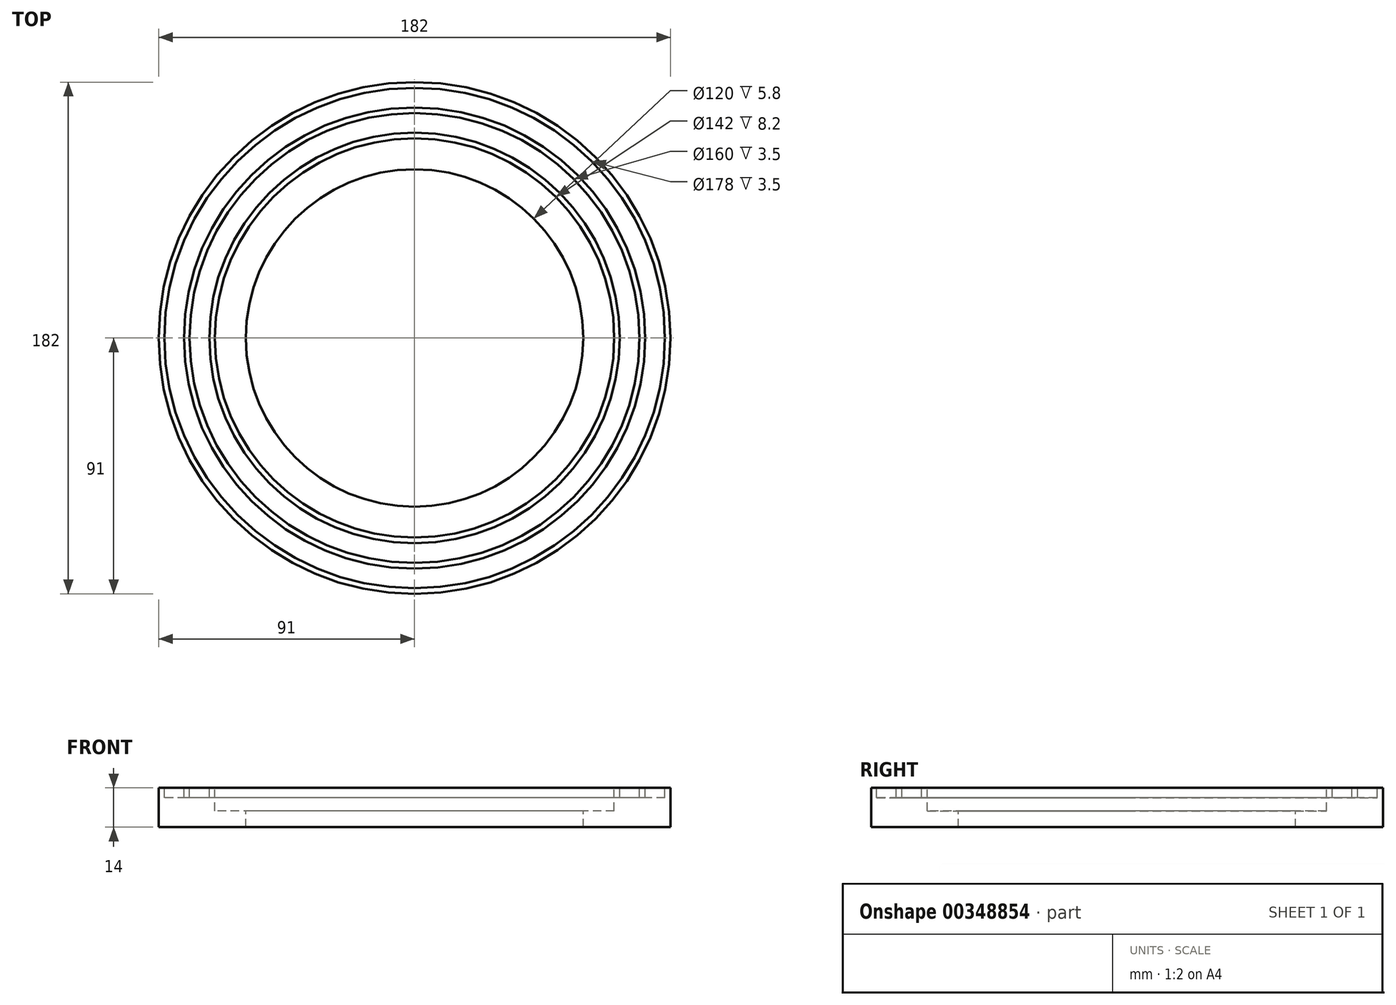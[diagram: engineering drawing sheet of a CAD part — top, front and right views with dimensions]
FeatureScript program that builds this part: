
annotation { "Feature Type Name" : "Feature", "Feature Type Description" : "" }
export const myFeature = defineFeature(function(context is Context, id is Id, definition is map)
    precondition{}
    {
        {
            var Q0;
            Q0=qCreatedBy(makeId("Front.planeOp"),FACE);
            var sketch = newSketch(context, id + "F0", { "sketchPlane" : qUnion([Q0])});
            skLineSegment(sketch, "E0", {"start": v(-60, 0) * mm, "end": v(-58.12, 0) * mm, "construction": true});
            skLineSegment(sketch, "E1", {"start": v(0, 63.7) * mm, "end": v(0, -49.54) * mm, "construction": true});
            skLineSegment(sketch, "E2", {"start": v(-60, 0) * mm, "end": v(-91, 0) * mm});
            skLineSegment(sketch, "E3", {"start": v(-91, 0) * mm, "end": v(-91, 14) * mm});
            skLineSegment(sketch, "E4", {"start": v(-91, 14) * mm, "end": v(-89, 14) * mm});
            skLineSegment(sketch, "E5", {"start": v(-89, 14) * mm, "end": v(-89, 10.5) * mm});
            skLineSegment(sketch, "E6", {"start": v(-89, 10.5) * mm, "end": v(-82, 10.5) * mm});
            skLineSegment(sketch, "E7", {"start": v(-82, 10.5) * mm, "end": v(-82, 14) * mm});
            skLineSegment(sketch, "E8", {"start": v(-82, 14) * mm, "end": v(-80, 14) * mm});
            skLineSegment(sketch, "E9", {"start": v(-80, 14) * mm, "end": v(-80, 10.5) * mm});
            skLineSegment(sketch, "E10", {"start": v(-80, 10.5) * mm, "end": v(-73, 10.5) * mm});
            skLineSegment(sketch, "E11", {"start": v(-73, 10.5) * mm, "end": v(-73, 14) * mm});
            skLineSegment(sketch, "E12", {"start": v(-73, 14) * mm, "end": v(-71, 14) * mm});
            skLineSegment(sketch, "E13", {"start": v(-71, 14) * mm, "end": v(-71, 5.8) * mm});
            skLineSegment(sketch, "E14", {"start": v(-71, 5.8) * mm, "end": v(-60, 5.8) * mm});
            skLineSegment(sketch, "E15", {"start": v(-60, 5.8) * mm, "end": v(-60, 0) * mm});
            skPoint(sketch, "E16.orphan", {"position": v(0, 5.8) * mm});
            skLineSegment(sketch, "E17.trimOffspring", {"start": v(0, 0) * mm, "end": v(50.9, 0) * mm, "construction": true});
            skSolve(sketch);
        }
        {
            var Q0;
            Q0=makeQuery(id+"F0.imprint","IMPRINT",FACE,{"disambiguationData":[TD([[makeQuery(id+"F0.imprint","IMPRINT",EDGE,{"derivedFrom":sQuery(id+"F0.wireOp",EDGE,"E2")}),-1.0]])]});
            var Q1;
            Q1=sQuery(id+"F0.wireOp",EDGE,"E1");
            revolve(context, id + "F1", {"entities" : qUnion([Q0]), "axis" : qUnion([Q1]), "revolveType" : RevolveType.FULL});
        }
    });
